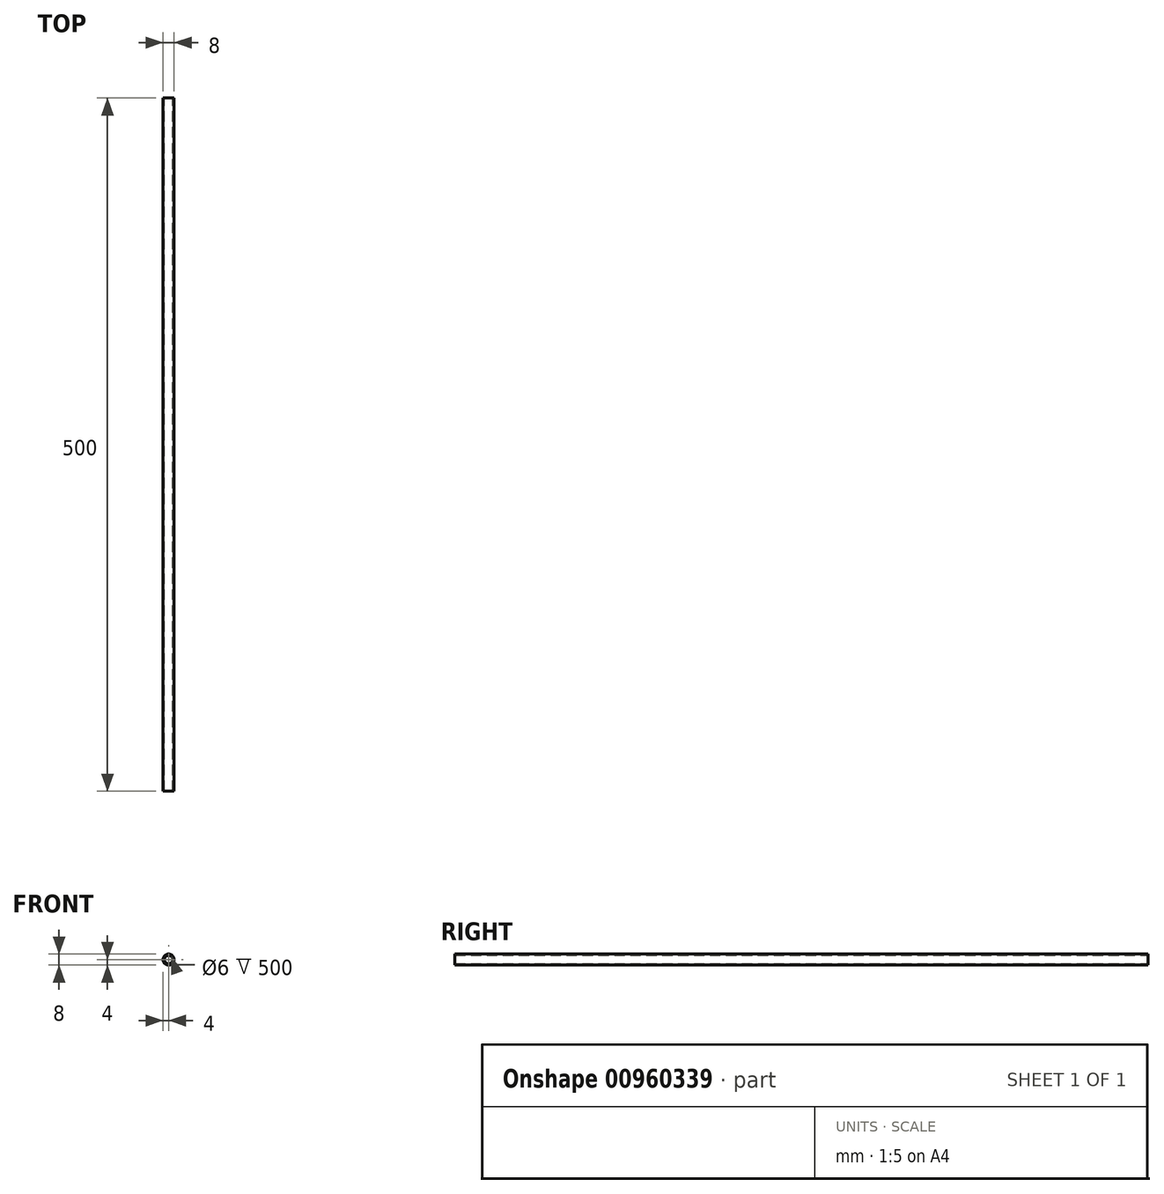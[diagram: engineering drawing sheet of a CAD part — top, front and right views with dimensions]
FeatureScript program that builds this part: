
annotation { "Feature Type Name" : "Feature", "Feature Type Description" : "" }
export const myFeature = defineFeature(function(context is Context, id is Id, definition is map)
    precondition{}
    {
        {
            var Q0;
            Q0=qCreatedBy(makeId("Front.planeOp"),FACE);
            var sketch = newSketch(context, id + "F0", { "sketchPlane" : qUnion([Q0])});
            skCircle(sketch, "E0", {"center": v(0, 0) * mm, "radius": 4 * mm});
            skCircle(sketch, "E1", {"center": v(0, 0) * mm, "radius": 3 * mm});
            skSolve(sketch);
        }
        {
            var Q0;
            Q0=makeQuery(id+"F0.imprint","IMPRINT",FACE,{"disambiguationData":[TD([[makeQuery(id+"F0.imprint","IMPRINT",EDGE,{"derivedFrom":sQuery(id+"F0.wireOp",EDGE,"E0")}),1.0]])]});
            extrude(context, id + "F1", {"entities" : qUnion([Q0]), "depth" : 500 * mm, "offsetDistance" : 25.4 * mm, "symmetric" : true});
        }
    });
